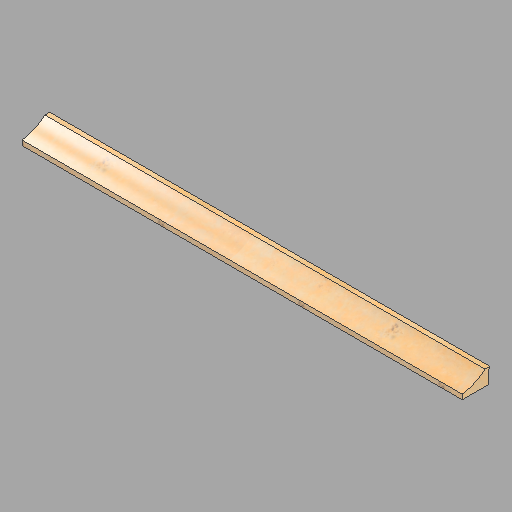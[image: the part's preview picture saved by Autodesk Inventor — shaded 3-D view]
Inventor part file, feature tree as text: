
AUTODESK INVENTOR PART (.ipt)
format: ipt  version: 2022.2 (Build 262287010, 287A)  size: 165,888 bytes
history: native  units: in
note: dims shown in document units (in); Inventor stores cm internally (conversion verified against a paired STEP export)
features: revolve x2, direct_edit x1, other x1
ambient origin geometry x8: Origin, YZ Plane, XZ Plane, XY Plane, X Axis, Y Axis, Z Axis, Center Point
bodies: Solid1 (feature_tree)
feature tree (4):
  direct_edit  "Direct Edit1"
  other  "Upper Jamb (1) (1)"
  revolve  "Rotate1"  [1 undecoded]
  revolve  "Rotate2"  [1 undecoded]
note: 2 required parameter values undecoded (feature->parameter linkage not recoverable at this tier; creation-order binding heuristic only, values carry confidence <= 0.55)
